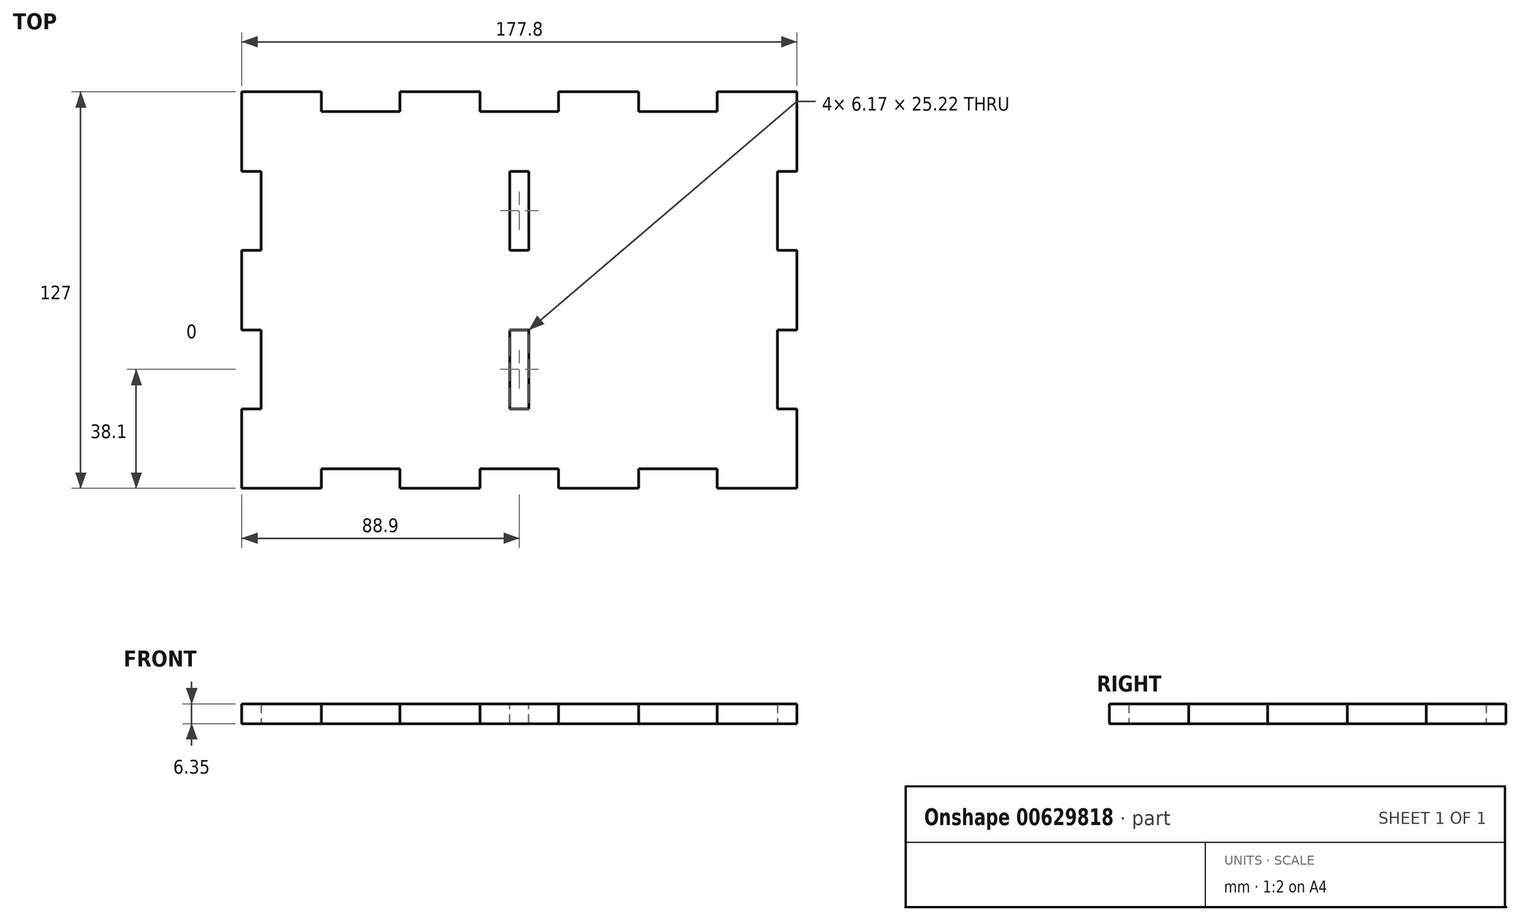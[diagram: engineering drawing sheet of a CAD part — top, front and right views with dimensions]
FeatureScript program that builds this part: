
annotation { "Feature Type Name" : "Feature", "Feature Type Description" : "" }
export const myFeature = defineFeature(function(context is Context, id is Id, definition is map)
    precondition{}
    {
        {
            var Q0;
            Q0=qCreatedBy(makeId("Top.planeOp"),FACE);
            var sketch = newSketch(context, id + "F0", { "sketchPlane" : qUnion([Q0])});
            skLineSegment(sketch, "E0.bottom", {"start": v(0, 0) * mm, "end": v(177.8, 0) * mm});
            skLineSegment(sketch, "E0.top", {"start": v(0, 127) * mm, "end": v(177.8, 127) * mm});
            skLineSegment(sketch, "E0.left", {"start": v(0, 0) * mm, "end": v(0, 127) * mm});
            skLineSegment(sketch, "E0.right", {"start": v(177.8, 0) * mm, "end": v(177.8, 127) * mm});
            skLineSegment(sketch, "E1.bottom", {"start": v(25.49, 0) * mm, "end": v(50.71, 0) * mm});
            skLineSegment(sketch, "E1.top", {"start": v(25.49, 6.26) * mm, "end": v(50.71, 6.26) * mm});
            skLineSegment(sketch, "E1.left", {"start": v(25.49, 0) * mm, "end": v(25.49, 6.26) * mm});
            skLineSegment(sketch, "E1.right", {"start": v(50.71, 0) * mm, "end": v(50.71, 6.26) * mm});
            skPoint(sketch, "E2", {"position": v(38.1, 6.26) * mm});
            skLineSegment(sketch, "E3.bottom", {"start": v(76.29, 0) * mm, "end": v(101.51, 0) * mm});
            skLineSegment(sketch, "E3.top", {"start": v(76.29, 6.26) * mm, "end": v(101.51, 6.26) * mm});
            skLineSegment(sketch, "E3.left", {"start": v(76.29, 0) * mm, "end": v(76.29, 6.26) * mm});
            skLineSegment(sketch, "E3.right", {"start": v(101.51, 0) * mm, "end": v(101.51, 6.26) * mm});
            skPoint(sketch, "E4", {"position": v(88.9, 6.26) * mm});
            skLineSegment(sketch, "E5.bottom", {"start": v(127.09, 0) * mm, "end": v(152.31, 0) * mm});
            skLineSegment(sketch, "E5.top", {"start": v(127.09, 6.26) * mm, "end": v(152.31, 6.26) * mm});
            skLineSegment(sketch, "E5.left", {"start": v(127.09, 0) * mm, "end": v(127.09, 6.26) * mm});
            skLineSegment(sketch, "E5.right", {"start": v(152.31, 0) * mm, "end": v(152.31, 6.26) * mm});
            skPoint(sketch, "E6", {"position": v(139.7, 6.26) * mm});
            skLineSegment(sketch, "E7.bottom", {"start": v(177.8, 25.49) * mm, "end": v(171.54, 25.49) * mm});
            skLineSegment(sketch, "E7.top", {"start": v(177.8, 50.71) * mm, "end": v(171.54, 50.71) * mm});
            skLineSegment(sketch, "E7.left", {"start": v(177.8, 25.49) * mm, "end": v(177.8, 50.71) * mm});
            skLineSegment(sketch, "E7.right", {"start": v(171.54, 25.49) * mm, "end": v(171.54, 50.71) * mm});
            skPoint(sketch, "E8", {"position": v(171.54, 38.1) * mm});
            skLineSegment(sketch, "E9.bottom", {"start": v(177.8, 76.29) * mm, "end": v(171.54, 76.29) * mm});
            skLineSegment(sketch, "E9.top", {"start": v(177.8, 101.51) * mm, "end": v(171.54, 101.51) * mm});
            skLineSegment(sketch, "E9.left", {"start": v(177.8, 76.29) * mm, "end": v(177.8, 101.51) * mm});
            skLineSegment(sketch, "E9.right", {"start": v(171.54, 76.29) * mm, "end": v(171.54, 101.51) * mm});
            skPoint(sketch, "E10", {"position": v(171.54, 88.9) * mm});
            skLineSegment(sketch, "E11", {"start": v(0, 63.5) * mm, "end": v(177.8, 63.5) * mm, "construction": true});
            skLineSegment(sketch, "E12", {"start": v(88.9, 127) * mm, "end": v(88.9, 0) * mm, "construction": true});
            skLineSegment(sketch, "E13.MirrorCS", {"start": v(50.71, 127) * mm, "end": v(50.71, 120.74) * mm});
            skLineSegment(sketch, "E14.MirrorCS", {"start": v(25.49, 120.74) * mm, "end": v(50.71, 120.74) * mm});
            skLineSegment(sketch, "E15.MirrorCS", {"start": v(25.49, 127) * mm, "end": v(50.71, 127) * mm});
            skLineSegment(sketch, "E16.MirrorCS", {"start": v(25.49, 127) * mm, "end": v(25.49, 120.74) * mm});
            skLineSegment(sketch, "E17.MirrorCS", {"start": v(101.51, 127) * mm, "end": v(101.51, 120.74) * mm});
            skLineSegment(sketch, "E18.MirrorCS", {"start": v(76.29, 120.74) * mm, "end": v(101.51, 120.74) * mm});
            skLineSegment(sketch, "E19.MirrorCS", {"start": v(76.29, 127) * mm, "end": v(76.29, 120.74) * mm});
            skLineSegment(sketch, "E20.MirrorCS", {"start": v(76.29, 127) * mm, "end": v(101.51, 127) * mm});
            skLineSegment(sketch, "E21.MirrorCS", {"start": v(127.09, 127) * mm, "end": v(127.09, 120.74) * mm});
            skLineSegment(sketch, "E22.MirrorCS", {"start": v(127.09, 120.74) * mm, "end": v(152.31, 120.74) * mm});
            skLineSegment(sketch, "E23.MirrorCS", {"start": v(127.09, 127) * mm, "end": v(152.31, 127) * mm});
            skLineSegment(sketch, "E24.MirrorCS", {"start": v(152.31, 127) * mm, "end": v(152.31, 120.74) * mm});
            skLineSegment(sketch, "E25.MirrorCS", {"start": v(0, 101.51) * mm, "end": v(6.26, 101.51) * mm});
            skLineSegment(sketch, "E26.MirrorCS", {"start": v(6.26, 76.29) * mm, "end": v(6.26, 101.51) * mm});
            skLineSegment(sketch, "E27.MirrorCS", {"start": v(0, 76.29) * mm, "end": v(6.26, 76.29) * mm});
            skLineSegment(sketch, "E28.MirrorCS", {"start": v(0, 76.29) * mm, "end": v(0, 101.51) * mm});
            skLineSegment(sketch, "E29.MirrorCS", {"start": v(0, 50.71) * mm, "end": v(6.26, 50.71) * mm});
            skLineSegment(sketch, "E30.MirrorCS", {"start": v(6.26, 25.49) * mm, "end": v(6.26, 50.71) * mm});
            skLineSegment(sketch, "E31.MirrorCS", {"start": v(0, 25.49) * mm, "end": v(6.26, 25.49) * mm});
            skLineSegment(sketch, "E32.MirrorCS", {"start": v(0, 25.49) * mm, "end": v(0, 50.71) * mm});
            skSolve(sketch);
        }
        {
            var Q0;
            Q0=makeQuery(id+"F0.imprint","IMPRINT",FACE,{"disambiguationData":[TD([[makeQuery(id+"F0.imprint","IMPRINT",EDGE,{"derivedFrom":sQuery(id+"F0.wireOp",EDGE,"E1.top")}),1.0]])]});
            extrude(context, id + "F1", {"entities" : qUnion([Q0]), "depth" : 6.35 * mm, "offsetDistance" : 25.4 * mm});
        }
        {
            var Q0;
            Q0=makeQuery(id+"F1.opExtrude","CAP_FACE",FACE,{"disambiguationData":[OSD([sQuery(id+"F0.wireOp",EDGE,"E0.bottom"),sQuery(id+"F0.wireOp",EDGE,"E0.top"),sQuery(id+"F0.wireOp",EDGE,"E0.left"),sQuery(id+"F0.wireOp",EDGE,"E0.right"),sQuery(id+"F0.wireOp",EDGE,"E1.top"),sQuery(id+"F0.wireOp",EDGE,"E1.left"),sQuery(id+"F0.wireOp",EDGE,"E1.right"),sQuery(id+"F0.wireOp",EDGE,"E3.top"),sQuery(id+"F0.wireOp",EDGE,"E3.left"),sQuery(id+"F0.wireOp",EDGE,"E3.right"),sQuery(id+"F0.wireOp",EDGE,"E5.top"),sQuery(id+"F0.wireOp",EDGE,"E5.left"),sQuery(id+"F0.wireOp",EDGE,"E5.right"),sQuery(id+"F0.wireOp",EDGE,"E7.bottom"),sQuery(id+"F0.wireOp",EDGE,"E7.top"),sQuery(id+"F0.wireOp",EDGE,"E7.right"),sQuery(id+"F0.wireOp",EDGE,"E9.bottom"),sQuery(id+"F0.wireOp",EDGE,"E9.top"),sQuery(id+"F0.wireOp",EDGE,"E9.right"),sQuery(id+"F0.wireOp",EDGE,"E13.MirrorCS"),sQuery(id+"F0.wireOp",EDGE,"E14.MirrorCS"),sQuery(id+"F0.wireOp",EDGE,"E16.MirrorCS"),sQuery(id+"F0.wireOp",EDGE,"E17.MirrorCS"),sQuery(id+"F0.wireOp",EDGE,"E18.MirrorCS"),sQuery(id+"F0.wireOp",EDGE,"E19.MirrorCS"),sQuery(id+"F0.wireOp",EDGE,"E21.MirrorCS"),sQuery(id+"F0.wireOp",EDGE,"E22.MirrorCS"),sQuery(id+"F0.wireOp",EDGE,"E24.MirrorCS"),sQuery(id+"F0.wireOp",EDGE,"E25.MirrorCS"),sQuery(id+"F0.wireOp",EDGE,"E26.MirrorCS"),sQuery(id+"F0.wireOp",EDGE,"E27.MirrorCS"),sQuery(id+"F0.wireOp",EDGE,"E29.MirrorCS"),sQuery(id+"F0.wireOp",EDGE,"E30.MirrorCS"),sQuery(id+"F0.wireOp",EDGE,"E31.MirrorCS")])],"isStart":false});
            var sketch = newSketch(context, id + "F2", { "sketchPlane" : qUnion([Q0])});
            skLineSegment(sketch, "E33.bottom", {"start": v(85.81, 101.51) * mm, "end": v(91.99, 101.51) * mm});
            skLineSegment(sketch, "E33.top", {"start": v(85.81, 76.29) * mm, "end": v(91.99, 76.29) * mm});
            skLineSegment(sketch, "E33.left", {"start": v(85.81, 101.51) * mm, "end": v(85.81, 76.29) * mm});
            skLineSegment(sketch, "E33.right", {"start": v(91.99, 101.51) * mm, "end": v(91.99, 76.29) * mm});
            skLineSegment(sketch, "E34.bottom", {"start": v(85.81, 50.71) * mm, "end": v(91.99, 50.71) * mm});
            skLineSegment(sketch, "E34.top", {"start": v(85.81, 25.49) * mm, "end": v(91.99, 25.49) * mm});
            skLineSegment(sketch, "E34.left", {"start": v(85.81, 50.71) * mm, "end": v(85.81, 25.49) * mm});
            skLineSegment(sketch, "E34.right", {"start": v(91.99, 50.71) * mm, "end": v(91.99, 25.49) * mm});
            skPoint(sketch, "E35", {"position": v(88.9, 25.49) * mm});
            skPoint(sketch, "E36", {"position": v(91.99, 38.1) * mm});
            skPoint(sketch, "E37", {"position": v(88.9, 76.29) * mm});
            skPoint(sketch, "E38", {"position": v(91.99, 88.9) * mm});
            skSolve(sketch);
        }
        {
            var Q0;
            Q0=makeQuery(id+"F2.imprint","IMPRINT",FACE,{"disambiguationData":[TD([[makeQuery(id+"F2.imprint","IMPRINT",EDGE,{"derivedFrom":sQuery(id+"F2.wireOp",EDGE,"E33.bottom")}),-1.0]])]});
            var Q1;
            Q1=makeQuery(id+"F2.imprint","IMPRINT",FACE,{"disambiguationData":[TD([[makeQuery(id+"F2.imprint","IMPRINT",EDGE,{"derivedFrom":sQuery(id+"F2.wireOp",EDGE,"E34.bottom")}),-1.0]])]});
            extrude(context, id + "F3", {"entities" : qUnion([Q0, Q1]), "operationType" : NewBodyOperationType.REMOVE, "endBound" : BoundingType.THROUGH_ALL, "oppositeDirection" : true, "depth" : 25.4 * mm, "offsetDistance" : 25.4 * mm});
        }
    });
